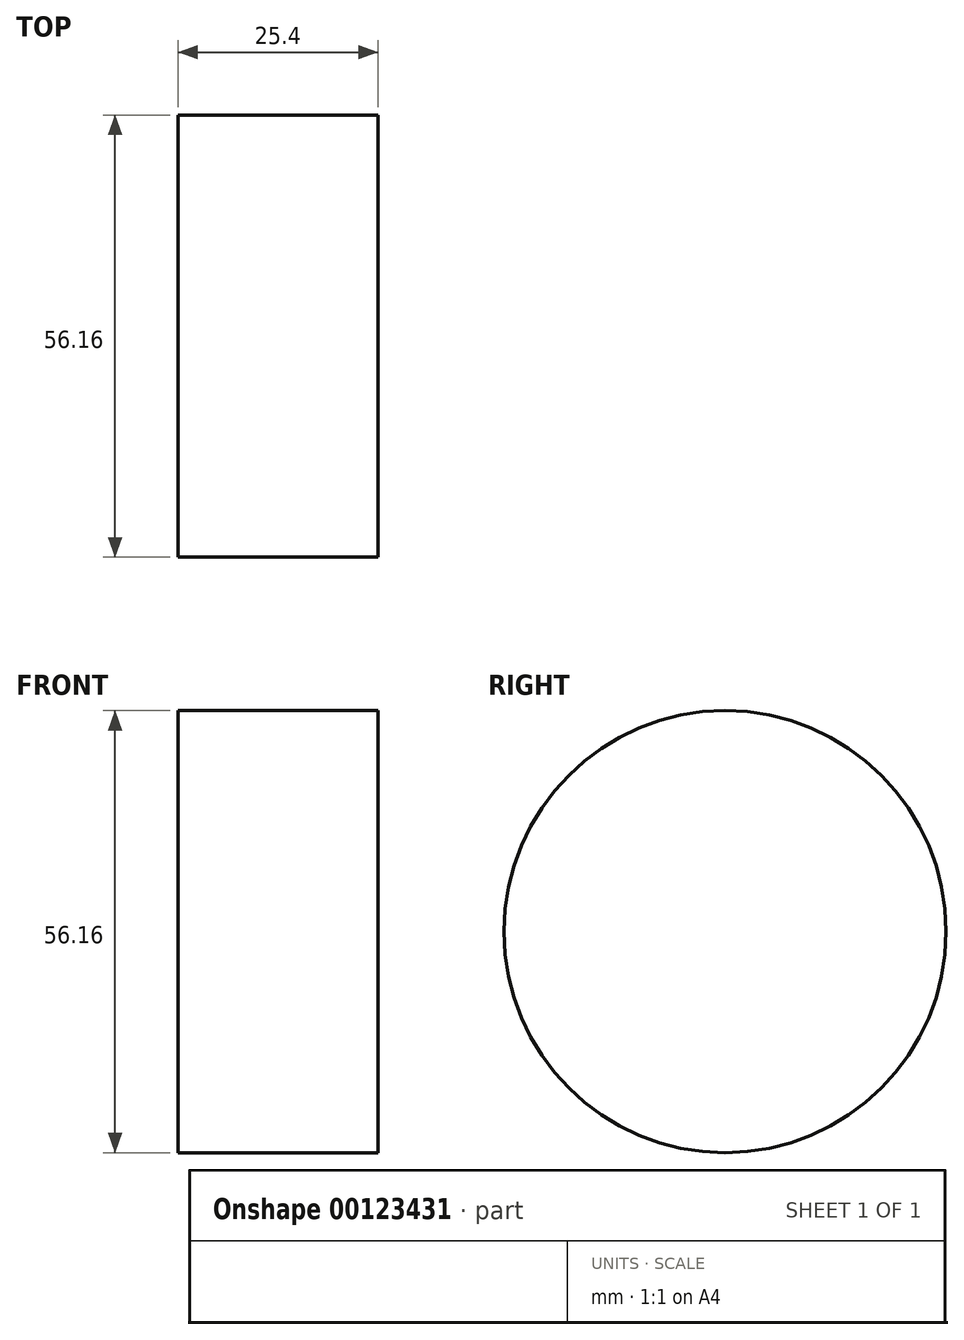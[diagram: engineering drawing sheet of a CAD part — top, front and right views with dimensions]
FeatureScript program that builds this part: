
annotation { "Feature Type Name" : "Feature", "Feature Type Description" : "" }
export const myFeature = defineFeature(function(context is Context, id is Id, definition is map)
    precondition{}
    {
        {
            var Q0;
            Q0=qCreatedBy(makeId("Right.planeOp"),FACE);
            var sketch = newSketch(context, id + "F0", { "sketchPlane" : qUnion([Q0])});
            skCircle(sketch, "E0", {"center": v(0, 0) * mm, "radius": 28.08 * mm});
            skSolve(sketch);
        }
        {
            var Q0;
            Q0=makeQuery(id+"F0.imprint","IMPRINT",FACE,{"disambiguationData":[TD([[makeQuery(id+"F0.imprint","IMPRINT",EDGE,{"derivedFrom":sQuery(id+"F0.wireOp",EDGE,"E0")}),1.0]])]});
            extrude(context, id + "F1", {"entities" : qUnion([Q0]), "depth" : 25.4 * mm});
        }
    });
